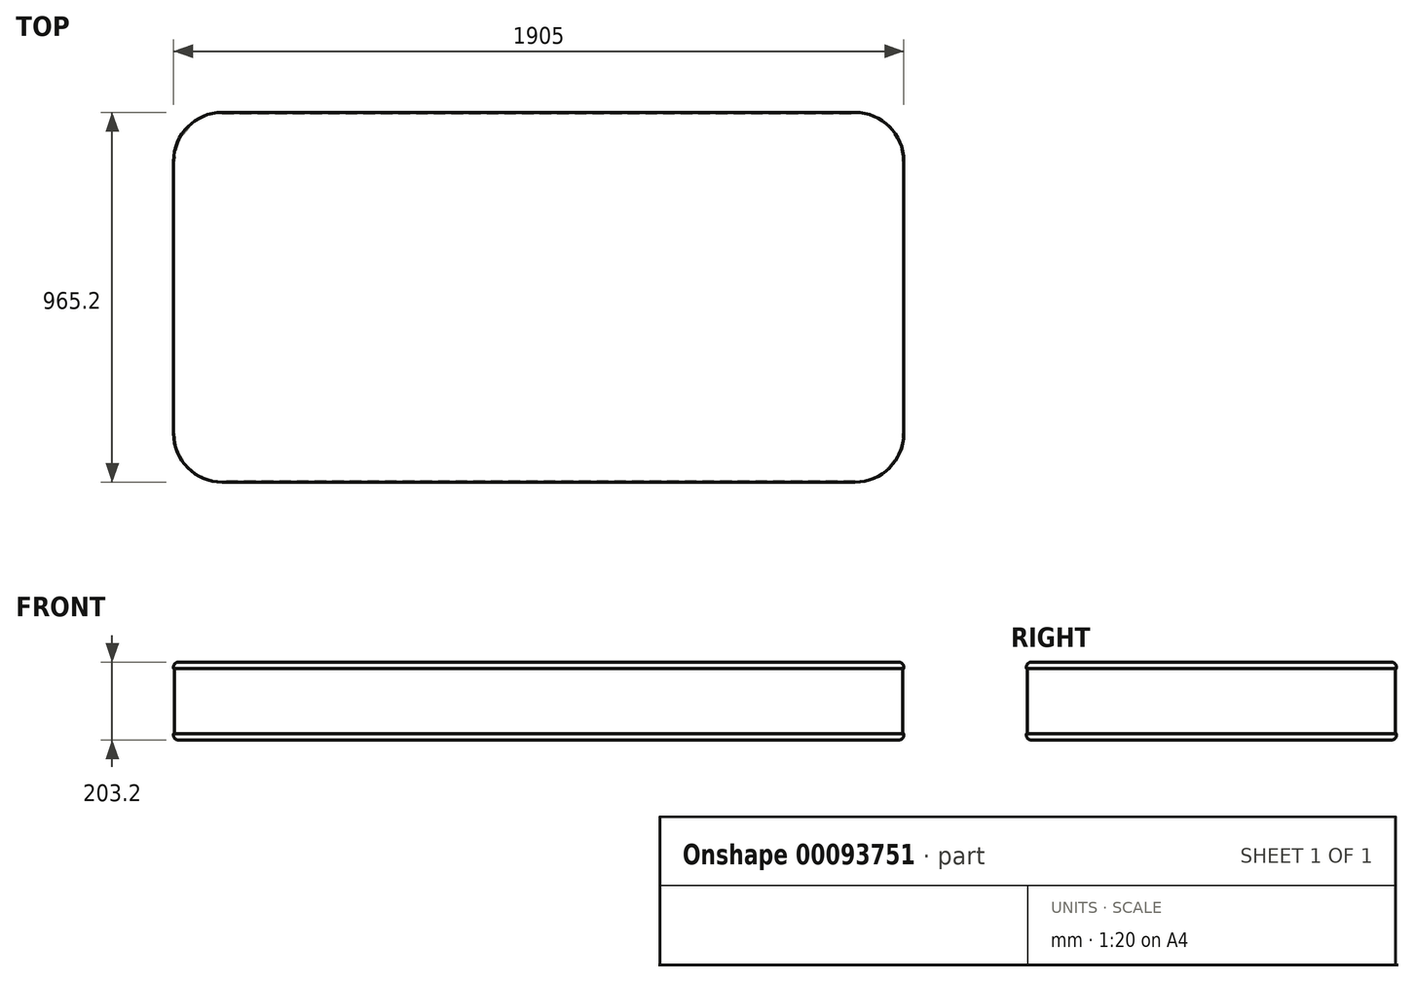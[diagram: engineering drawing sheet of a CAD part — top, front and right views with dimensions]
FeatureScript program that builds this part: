
annotation { "Feature Type Name" : "Feature", "Feature Type Description" : "" }
export const myFeature = defineFeature(function(context is Context, id is Id, definition is map)
    precondition{}
    {
        {
            var Q0;
            Q0=qCreatedBy(makeId("Top.planeOp"),FACE);
            var sketch = newSketch(context, id + "F0", { "sketchPlane" : qUnion([Q0])});
            skLineSegment(sketch, "E0.bottom", {"start": v(952.5, 482.6) * mm, "end": v(-952.5, 482.6) * mm});
            skLineSegment(sketch, "E0.top", {"start": v(952.5, -482.6) * mm, "end": v(-952.5, -482.6) * mm});
            skLineSegment(sketch, "E0.left", {"start": v(952.5, 482.6) * mm, "end": v(952.5, -482.6) * mm});
            skLineSegment(sketch, "E0.right", {"start": v(-952.5, 482.6) * mm, "end": v(-952.5, -482.6) * mm});
            skPoint(sketch, "E0.middle", {"position": v(0, 0) * mm});
            skSolve(sketch);
        }
        {
            var Q0;
            Q0=makeQuery(id+"F0.imprint","IMPRINT",FACE,{"disambiguationData":[TD([[makeQuery(id+"F0.imprint","IMPRINT",EDGE,{"derivedFrom":sQuery(id+"F0.wireOp",EDGE,"E0.bottom")}),1.0]])]});
            extrude(context, id + "F1", {"entities" : qUnion([Q0]), "depth" : 203.2 * mm});
        }
        {
            var Q0;
            Q0=makeQuery(id+"F1.opExtrude","SWEPT_EDGE",EDGE,{"disambiguationData":[OSD([sQuery(id+"F0.wireOp",EDGE,"E0.top"),sQuery(id+"F0.wireOp",EDGE,"E0.left")])]});
            var Q1;
            Q1=makeQuery(id+"F1.opExtrude","SWEPT_EDGE",EDGE,{"disambiguationData":[OSD([sQuery(id+"F0.wireOp",EDGE,"E0.top"),sQuery(id+"F0.wireOp",EDGE,"E0.right")])]});
            var Q2;
            Q2=makeQuery(id+"F1.opExtrude","SWEPT_EDGE",EDGE,{"disambiguationData":[OSD([sQuery(id+"F0.wireOp",EDGE,"E0.bottom"),sQuery(id+"F0.wireOp",EDGE,"E0.left")])]});
            var Q3;
            Q3=makeQuery(id+"F1.opExtrude","SWEPT_EDGE",EDGE,{"disambiguationData":[OSD([sQuery(id+"F0.wireOp",EDGE,"E0.bottom"),sQuery(id+"F0.wireOp",EDGE,"E0.right")])]});
            fillet(context, id + "F2", {"entities" : qUnion([Q0, Q1, Q2, Q3]), "radius" : 127 * mm, "tangentPropagation" : true, "allowEdgeOverflow" : false});
        }
        {
            var Q0;
            Q0=makeQuery(id+"F1.opExtrude","CAP_FACE",FACE,{"disambiguationData":[OSD([sQuery(id+"F0.wireOp",EDGE,"E0.bottom"),sQuery(id+"F0.wireOp",EDGE,"E0.top"),sQuery(id+"F0.wireOp",EDGE,"E0.left"),sQuery(id+"F0.wireOp",EDGE,"E0.right")])],"isStart":false});
            var Q1;
            Q1=makeQuery(id+"F1.opExtrude","CAP_FACE",FACE,{"disambiguationData":[OSD([sQuery(id+"F0.wireOp",EDGE,"E0.bottom"),sQuery(id+"F0.wireOp",EDGE,"E0.top"),sQuery(id+"F0.wireOp",EDGE,"E0.left"),sQuery(id+"F0.wireOp",EDGE,"E0.right")])],"isStart":true});
            fillet(context, id + "F3", {"entities" : qUnion([Q0, Q1]), "radius" : 12.7 * mm, "tangentPropagation" : true, "allowEdgeOverflow" : false});
        }
        {
            var Q0;
            Q0=makeQuery(id+"F1.opExtrude","SWEPT_FACE",FACE,{"disambiguationData":[OSD([sQuery(id+"F0.wireOp",EDGE,"E0.left")])]});
            var Q1;
            {var subQ0=sQuery(id+"F0.wireOp",EDGE,"E0.top");var subQ1=sQuery(id+"F0.wireOp",EDGE,"E0.left");Q1=makeQuery(id+"F3.opFillet","BLEND_VERTEX",VERTEX,{"blendedFrom":[makeQuery(id+"F2.opFillet","BLEND_EDGE",EDGE,{"blendedFrom":[makeQuery(id+"F1.opExtrude","SWEPT_EDGE",EDGE,{"disambiguationData":[OSD([subQ0,subQ1])]}),makeQuery(id+"F1.opExtrude","CAP_FACE",FACE,{"disambiguationData":[OSD([sQuery(id+"F0.wireOp",EDGE,"E0.bottom"),subQ0,subQ1,sQuery(id+"F0.wireOp",EDGE,"E0.right")])],"isStart":false})],"blendedInto":[makeQuery(id+"F1.opExtrude","CAP_FACE",FACE,{"disambiguationData":[OSD([sQuery(id+"F0.wireOp",EDGE,"E0.bottom"),subQ0,subQ1,sQuery(id+"F0.wireOp",EDGE,"E0.right")])],"isStart":false})]}),makeQuery(id+"F1.opExtrude","CAP_EDGE",EDGE,{"disambiguationData":[OSD([subQ0])],"isStart":false}),makeQuery(id+"F2.opFillet","BLEND_FACE",FACE,{"disambiguationData":[OSD([subQ0,subQ1])]}),makeQuery(id+"F1.opExtrude","SWEPT_FACE",FACE,{"disambiguationData":[OSD([subQ0])]})],"blendedInto":[makeQuery(id+"F2.opFillet","BLEND_FACE",FACE,{"disambiguationData":[OSD([subQ0,subQ1])]}),makeQuery(id+"F1.opExtrude","SWEPT_FACE",FACE,{"disambiguationData":[OSD([subQ0])]})]});}
            cPlane(context, id + "F4", {"entities" : qUnion([Q0, Q1]), "cplaneType" : CPlaneType.PLANE_POINT, "offset" : 152.4 * mm, "width" : 152.4 * mm, "height" : 152.4 * mm});
        }
        {
            var Q0;
            Q0=qCreatedBy(id+"F4.planeOp",FACE);
            var sketch = newSketch(context, id + "F5", { "sketchPlane" : qUnion([Q0])});
            skLineSegment(sketch, "E1", {"start": v(-480.06, 182.14) * mm, "end": v(-480.06, 21.06) * mm});
            skLineSegment(sketch, "E2", {"start": v(-485.86, 14.73) * mm, "end": v(-553.35, 8.83) * mm});
            skLineSegment(sketch, "E3", {"start": v(-553.35, 8.83) * mm, "end": v(-553.35, 194.37) * mm});
            skLineSegment(sketch, "E4", {"start": v(-553.35, 194.37) * mm, "end": v(-485.86, 188.47) * mm});
            skLineSegment(sketch, "E5", {"start": v(-482.6, 101.6) * mm, "end": v(-480.06, 101.6) * mm, "construction": true});
            skPoint(sketch, "E6.visualSharp", {"position": v(-480.06, 187.96) * mm});
            skArc(sketch, "E6.filletArc", {"start": v(-480.06, 182.14) * mm, "mid": v(-481.73, 186.43) * mm, "end": v(-485.86, 188.47) * mm});
            skPoint(sketch, "E7.visualSharp", {"position": v(-480.06, 15.24) * mm});
            skArc(sketch, "E7.filletArc", {"start": v(-485.86, 14.73) * mm, "mid": v(-481.73, 16.77) * mm, "end": v(-480.06, 21.06) * mm});
            skSolve(sketch);
        }
        {
            var Q0;
            Q0=makeQuery(id+"F1.opExtrude","CAP_FACE",FACE,{"disambiguationData":[OSD([sQuery(id+"F0.wireOp",EDGE,"E0.bottom"),sQuery(id+"F0.wireOp",EDGE,"E0.top"),sQuery(id+"F0.wireOp",EDGE,"E0.left"),sQuery(id+"F0.wireOp",EDGE,"E0.right")])],"isStart":false});
            var Q1;
            Q1=sQuery(id+"F5.wireOp",VERTEX,"E5.start");
            cPlane(context, id + "F6", {"entities" : qUnion([Q0, Q1]), "cplaneType" : CPlaneType.PLANE_POINT, "offset" : 152.4 * mm, "width" : 152.4 * mm, "height" : 152.4 * mm});
        }
        {
            var Q0;
            Q0=makeQuery(id+"F5.imprint","IMPRINT",FACE,{"disambiguationData":[TD([[makeQuery(id+"F5.imprint","IMPRINT",EDGE,{"derivedFrom":sQuery(id+"F5.wireOp",EDGE,"E1")}),-1.0]])]});
            var Q1;
            {var subQ0=sQuery(id+"F0.wireOp",EDGE,"E0.top");Q1=makeQuery(id+"F3.opFillet","BLEND_EDGE",EDGE,{"blendedFrom":[makeQuery(id+"F1.opExtrude","CAP_EDGE",EDGE,{"disambiguationData":[OSD([subQ0])],"isStart":false}),makeQuery(id+"F1.opExtrude","SWEPT_FACE",FACE,{"disambiguationData":[OSD([subQ0])]})],"blendedInto":[makeQuery(id+"F1.opExtrude","SWEPT_FACE",FACE,{"disambiguationData":[OSD([subQ0])]})]});}
            var Q2;
            {var subQ0=sQuery(id+"F0.wireOp",EDGE,"E0.right");var subQ1=sQuery(id+"F0.wireOp",EDGE,"E0.top");Q2=makeQuery(id+"F3.opFillet","BLEND_EDGE",EDGE,{"blendedFrom":[makeQuery(id+"F2.opFillet","BLEND_EDGE",EDGE,{"blendedFrom":[makeQuery(id+"F1.opExtrude","SWEPT_EDGE",EDGE,{"disambiguationData":[OSD([subQ1,subQ0])]}),makeQuery(id+"F1.opExtrude","CAP_FACE",FACE,{"disambiguationData":[OSD([sQuery(id+"F0.wireOp",EDGE,"E0.bottom"),subQ1,sQuery(id+"F0.wireOp",EDGE,"E0.left"),subQ0])],"isStart":false})],"blendedInto":[makeQuery(id+"F1.opExtrude","CAP_FACE",FACE,{"disambiguationData":[OSD([sQuery(id+"F0.wireOp",EDGE,"E0.bottom"),subQ1,sQuery(id+"F0.wireOp",EDGE,"E0.left"),subQ0])],"isStart":false})]}),makeQuery(id+"F2.opFillet","BLEND_FACE",FACE,{"disambiguationData":[OSD([subQ1,subQ0])]})],"blendedInto":[makeQuery(id+"F2.opFillet","BLEND_FACE",FACE,{"disambiguationData":[OSD([subQ1,subQ0])]})]});}
            var Q3;
            {var subQ0=sQuery(id+"F0.wireOp",EDGE,"E0.right");Q3=makeQuery(id+"F3.opFillet","BLEND_EDGE",EDGE,{"blendedFrom":[makeQuery(id+"F1.opExtrude","CAP_EDGE",EDGE,{"disambiguationData":[OSD([subQ0])],"isStart":false}),makeQuery(id+"F1.opExtrude","SWEPT_FACE",FACE,{"disambiguationData":[OSD([subQ0])]})],"blendedInto":[makeQuery(id+"F1.opExtrude","SWEPT_FACE",FACE,{"disambiguationData":[OSD([subQ0])]})]});}
            var Q4;
            {var subQ0=sQuery(id+"F0.wireOp",EDGE,"E0.right");var subQ1=sQuery(id+"F0.wireOp",EDGE,"E0.bottom");Q4=makeQuery(id+"F3.opFillet","BLEND_EDGE",EDGE,{"blendedFrom":[makeQuery(id+"F2.opFillet","BLEND_EDGE",EDGE,{"blendedFrom":[makeQuery(id+"F1.opExtrude","SWEPT_EDGE",EDGE,{"disambiguationData":[OSD([subQ1,subQ0])]}),makeQuery(id+"F1.opExtrude","CAP_FACE",FACE,{"disambiguationData":[OSD([subQ1,sQuery(id+"F0.wireOp",EDGE,"E0.top"),sQuery(id+"F0.wireOp",EDGE,"E0.left"),subQ0])],"isStart":false})],"blendedInto":[makeQuery(id+"F1.opExtrude","CAP_FACE",FACE,{"disambiguationData":[OSD([subQ1,sQuery(id+"F0.wireOp",EDGE,"E0.top"),sQuery(id+"F0.wireOp",EDGE,"E0.left"),subQ0])],"isStart":false})]}),makeQuery(id+"F2.opFillet","BLEND_FACE",FACE,{"disambiguationData":[OSD([subQ1,subQ0])]})],"blendedInto":[makeQuery(id+"F2.opFillet","BLEND_FACE",FACE,{"disambiguationData":[OSD([subQ1,subQ0])]})]});}
            var Q5;
            {var subQ0=sQuery(id+"F0.wireOp",EDGE,"E0.bottom");Q5=makeQuery(id+"F3.opFillet","BLEND_EDGE",EDGE,{"blendedFrom":[makeQuery(id+"F1.opExtrude","CAP_EDGE",EDGE,{"disambiguationData":[OSD([subQ0])],"isStart":false}),makeQuery(id+"F1.opExtrude","SWEPT_FACE",FACE,{"disambiguationData":[OSD([subQ0])]})],"blendedInto":[makeQuery(id+"F1.opExtrude","SWEPT_FACE",FACE,{"disambiguationData":[OSD([subQ0])]})]});}
            var Q6;
            {var subQ0=sQuery(id+"F0.wireOp",EDGE,"E0.left");var subQ1=sQuery(id+"F0.wireOp",EDGE,"E0.bottom");Q6=makeQuery(id+"F3.opFillet","BLEND_EDGE",EDGE,{"blendedFrom":[makeQuery(id+"F2.opFillet","BLEND_EDGE",EDGE,{"blendedFrom":[makeQuery(id+"F1.opExtrude","SWEPT_EDGE",EDGE,{"disambiguationData":[OSD([subQ1,subQ0])]}),makeQuery(id+"F1.opExtrude","CAP_FACE",FACE,{"disambiguationData":[OSD([subQ1,sQuery(id+"F0.wireOp",EDGE,"E0.top"),subQ0,sQuery(id+"F0.wireOp",EDGE,"E0.right")])],"isStart":false})],"blendedInto":[makeQuery(id+"F1.opExtrude","CAP_FACE",FACE,{"disambiguationData":[OSD([subQ1,sQuery(id+"F0.wireOp",EDGE,"E0.top"),subQ0,sQuery(id+"F0.wireOp",EDGE,"E0.right")])],"isStart":false})]}),makeQuery(id+"F2.opFillet","BLEND_FACE",FACE,{"disambiguationData":[OSD([subQ1,subQ0])]})],"blendedInto":[makeQuery(id+"F2.opFillet","BLEND_FACE",FACE,{"disambiguationData":[OSD([subQ1,subQ0])]})]});}
            var Q7;
            {var subQ0=sQuery(id+"F0.wireOp",EDGE,"E0.left");Q7=makeQuery(id+"F3.opFillet","BLEND_EDGE",EDGE,{"blendedFrom":[makeQuery(id+"F1.opExtrude","CAP_EDGE",EDGE,{"disambiguationData":[OSD([subQ0])],"isStart":false}),makeQuery(id+"F1.opExtrude","SWEPT_FACE",FACE,{"disambiguationData":[OSD([subQ0])]})],"blendedInto":[makeQuery(id+"F1.opExtrude","SWEPT_FACE",FACE,{"disambiguationData":[OSD([subQ0])]})]});}
            var Q8;
            {var subQ0=sQuery(id+"F0.wireOp",EDGE,"E0.left");var subQ1=sQuery(id+"F0.wireOp",EDGE,"E0.top");Q8=makeQuery(id+"F3.opFillet","BLEND_EDGE",EDGE,{"blendedFrom":[makeQuery(id+"F2.opFillet","BLEND_EDGE",EDGE,{"blendedFrom":[makeQuery(id+"F1.opExtrude","SWEPT_EDGE",EDGE,{"disambiguationData":[OSD([subQ1,subQ0])]}),makeQuery(id+"F1.opExtrude","CAP_FACE",FACE,{"disambiguationData":[OSD([sQuery(id+"F0.wireOp",EDGE,"E0.bottom"),subQ1,subQ0,sQuery(id+"F0.wireOp",EDGE,"E0.right")])],"isStart":false})],"blendedInto":[makeQuery(id+"F1.opExtrude","CAP_FACE",FACE,{"disambiguationData":[OSD([sQuery(id+"F0.wireOp",EDGE,"E0.bottom"),subQ1,subQ0,sQuery(id+"F0.wireOp",EDGE,"E0.right")])],"isStart":false})]}),makeQuery(id+"F2.opFillet","BLEND_FACE",FACE,{"disambiguationData":[OSD([subQ1,subQ0])]})],"blendedInto":[makeQuery(id+"F2.opFillet","BLEND_FACE",FACE,{"disambiguationData":[OSD([subQ1,subQ0])]})]});}
            sweep(context, id + "F7", {"operationType" : NewBodyOperationType.REMOVE, "profiles" : qUnion([Q0]), "path" : qUnion([Q1, Q2, Q3, Q4, Q5, Q6, Q7, Q8])});
        }
    });
